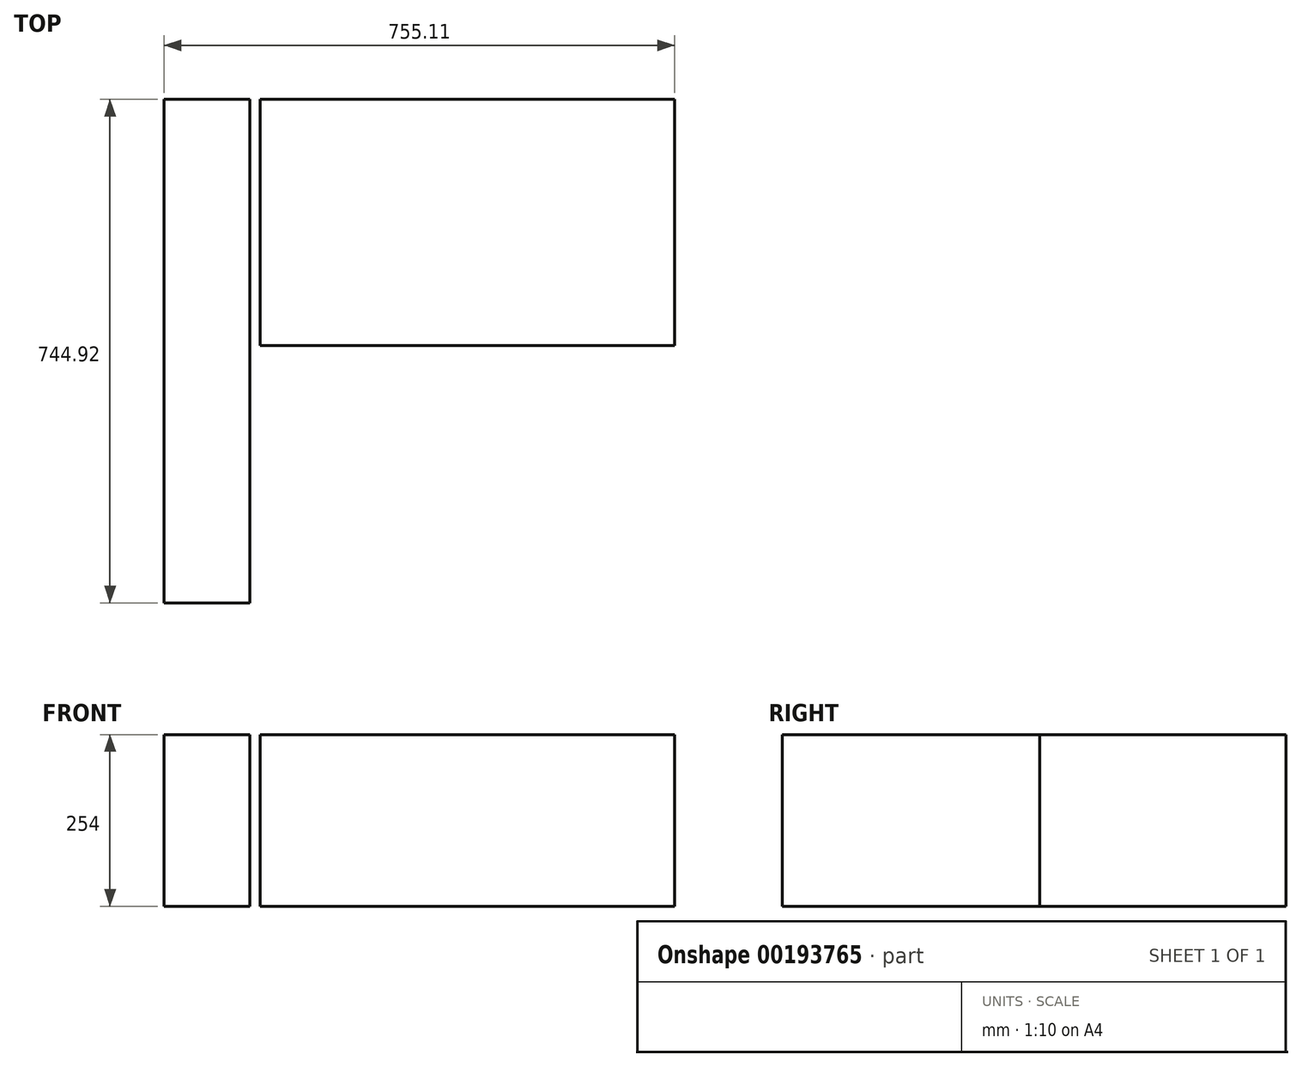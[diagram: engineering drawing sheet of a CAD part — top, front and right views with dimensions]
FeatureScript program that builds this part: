
annotation { "Feature Type Name" : "Feature", "Feature Type Description" : "" }
export const myFeature = defineFeature(function(context is Context, id is Id, definition is map)
    precondition{}
    {
        {
            var Q0;
            Q0=qCreatedBy(makeId("Top.planeOp"),FACE);
            var sketch = newSketch(context, id + "F0", { "sketchPlane" : qUnion([Q0])});
            skLineSegment(sketch, "E0.bottom", {"start": v(306.62, 181.96) * mm, "end": v(-306.62, 181.96) * mm});
            skLineSegment(sketch, "E0.top", {"start": v(306.62, -181.96) * mm, "end": v(-306.62, -181.96) * mm});
            skLineSegment(sketch, "E0.left", {"start": v(306.62, 181.96) * mm, "end": v(306.62, -181.96) * mm});
            skLineSegment(sketch, "E0.right", {"start": v(-306.62, 181.96) * mm, "end": v(-306.62, -181.96) * mm});
            skPoint(sketch, "E0.middle", {"position": v(0, 0) * mm});
            skLineSegment(sketch, "E1.bottom", {"start": v(-448.5, 181.96) * mm, "end": v(-321.5, 181.96) * mm});
            skLineSegment(sketch, "E1.top", {"start": v(-448.5, -181.96) * mm, "end": v(-321.5, -181.96) * mm});
            skLineSegment(sketch, "E1.left", {"start": v(-448.5, 181.96) * mm, "end": v(-448.5, -181.96) * mm});
            skLineSegment(sketch, "E1.right", {"start": v(-321.5, 181.96) * mm, "end": v(-321.5, -181.96) * mm});
            skSolve(sketch);
        }
        {
            var Q0;
            Q0=makeQuery(id+"F0.imprint","IMPRINT",FACE,{"disambiguationData":[TD([[makeQuery(id+"F0.imprint","IMPRINT",EDGE,{"derivedFrom":sQuery(id+"F0.wireOp",EDGE,"E1.bottom")}),-1.0]])]});
            var Q1;
            Q1=makeQuery(id+"F0.imprint","IMPRINT",FACE,{"disambiguationData":[TD([[makeQuery(id+"F0.imprint","IMPRINT",EDGE,{"derivedFrom":sQuery(id+"F0.wireOp",EDGE,"E0.bottom")}),1.0]])]});
            extrude(context, id + "F1", {"entities" : qUnion([Q0, Q1]), "depth" : 254 * mm});
        }
        {
            var Q0;
            Q0=makeQuery(id+"F1.opExtrude","SWEPT_FACE",FACE,{"disambiguationData":[OSD([sQuery(id+"F0.wireOp",EDGE,"E1.top")])]});
            extrude(context, id + "F2", {"entities" : qUnion([Q0]), "operationType" : NewBodyOperationType.ADD, "depth" : 381 * mm});
        }
    });
